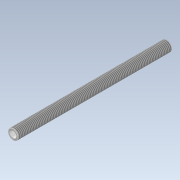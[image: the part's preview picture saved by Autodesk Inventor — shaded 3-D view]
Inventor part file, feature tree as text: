
AUTODESK INVENTOR PART (.ipt)
format: ipt  version: 2021 (Build 250183000, 183)  size: 95,232 bytes
history: native  units: mm
features: other x1, revolve x1, thread x1, chamfer x1, sketch x1
ambient origin geometry x8: Origin, YZ Plane, XZ Plane, XY Plane, X Axis, Y Axis, Z Axis, Center Point
bodies: Body1 (feature_tree)
feature tree (5):
  other  "Sólido1"
  revolve  "Revolución1"  [1 undecoded]
  thread  "Rosca1"  [1 undecoded]
  chamfer  "Chaflán1"  Angle=90.0deg  [1 undecoded]
  sketch  "Boceto1"  dims[d0=150.0mm d1=10.0mm d3=2.0mm d4=90.0deg d5=100.0mm d6=0.0mm d7=0.5mm d8=2.0mm d9=45.0deg]
note: 3 required parameter values undecoded (feature->parameter linkage not recoverable at this tier; creation-order binding heuristic only, values carry confidence <= 0.55)